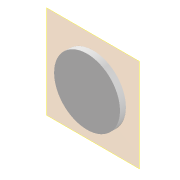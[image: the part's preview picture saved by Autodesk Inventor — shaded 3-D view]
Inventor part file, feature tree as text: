
AUTODESK INVENTOR PART (.ipt)
format: ipt  version: 2021 (Build 250183000, 183)  size: 89,600 bytes
history: native  units: in
note: dims shown in document units (in); Inventor stores cm internally (conversion verified against a paired STEP export)
features: plane x1, extrude x1, sketch x1
ambient origin geometry x8: Origin, YZ Plane, XZ Plane, XY Plane, X Axis, Y Axis, Z Axis, Center Point
bodies: Solid1 (feature_tree)
feature tree (3):
  plane  "Work Plane1"
  extrude  "Extrusion1"  Depth=0.3937in TaperAngle=0.0deg
  sketch  "Sketch1"  dims[d0=4.3701in d1=0.3937in d2=0.0in]
